# Revit family: Zumtobel SUPIL
name_source: partatom
category: Lighting Fixtures
revit_build: Autodesk Revit 2016 (Build: 20150220_1215(x64)
units: mm (PartAtom-declared; Revit-internal decimal feet)

## family parameters
Always vertical = Yes
Cut with Voids When Loaded = No
Light Source = Yes
OmniClass Number = 23.80.70.00
OmniClass Title = Lighting
Part Type = Normal
Room Calculation Point = No
Round Connector Dimension = Use Diameter
Shared = No
Work Plane-Based = No

## types (1)
- SUPIL-R DF6 2000-930 LDO FL-DBK LH40 BK
    Apparent Load = 25 VA
    Color Filter = 16777215
    Dimming Lamp Color Temperature Shift = <None>
    Emit Shape Visible in Rendering = No
    Emit from Rectangle Length = 38 mm  [stored 0.124672 ft]
    Emit from Rectangle Width = 218 mm  [stored 0.715223 ft]
    Height = 101 mm  [stored 0.331365 ft]
    Lamp = LED
    Length = 218 mm  [stored 0.715223 ft]
    Manufacturer = Zumtobel Lighting
    Model = 60211113
    Photometric Web File = 60211113_(STD_LEO).IES
    Tilt Angle = 90.00°
    URL = http://www.zumtobel.com
    Voltage = 230 V
    Width = 38 mm  [stored 0.124672 ft]

note: [stored X ft] marks values corroborated as IEEE doubles in the binary element streams (Revit-internal decimal feet)

## geometry (parser evidence)
native form markers: Sweep x2
no freeform markers — native parametric forms only
